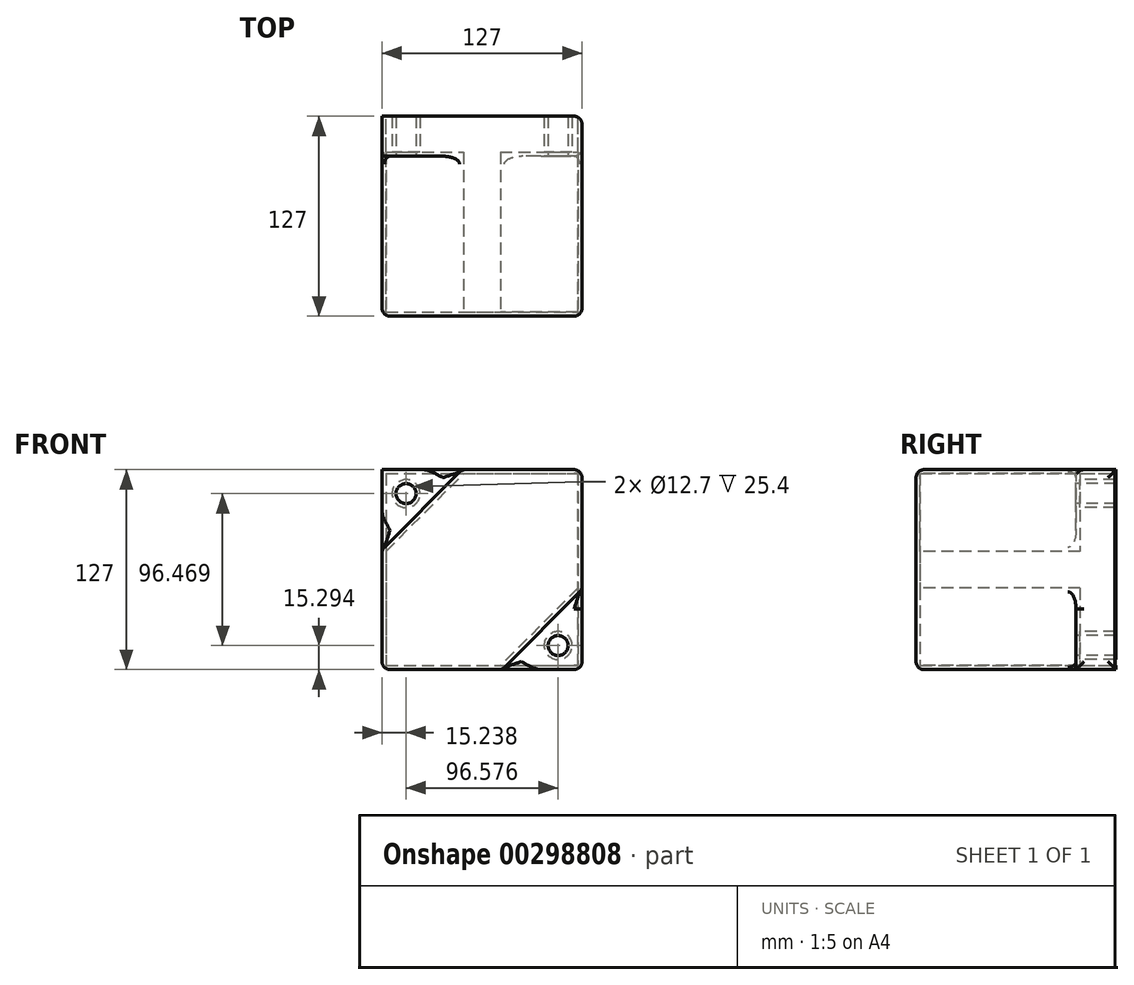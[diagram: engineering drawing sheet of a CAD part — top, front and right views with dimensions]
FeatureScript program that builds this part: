
annotation { "Feature Type Name" : "Feature", "Feature Type Description" : "" }
export const myFeature = defineFeature(function(context is Context, id is Id, definition is map)
    precondition{}
    {
        {
            var Q0;
            Q0=qCreatedBy(makeId("Front.planeOp"),FACE);
            var sketch = newSketch(context, id + "F0", { "sketchPlane" : qUnion([Q0])});
            skLineSegment(sketch, "E0.bottom", {"start": v(-56.8, 80.98) * mm, "end": v(70.2, 80.98) * mm});
            skLineSegment(sketch, "E0.top", {"start": v(-56.8, -46.02) * mm, "end": v(70.2, -46.02) * mm});
            skLineSegment(sketch, "E0.left", {"start": v(-56.8, 80.98) * mm, "end": v(-56.8, -46.02) * mm});
            skLineSegment(sketch, "E0.right", {"start": v(70.2, 80.98) * mm, "end": v(70.2, -46.02) * mm});
            skSolve(sketch);
        }
        {
            var Q0;
            Q0=makeQuery(id+"F0.imprint","IMPRINT",FACE,{"disambiguationData":[TD([[makeQuery(id+"F0.imprint","IMPRINT",EDGE,{"derivedFrom":sQuery(id+"F0.wireOp",EDGE,"E0.bottom")}),-1.0]])]});
            extrude(context, id + "F1", {"entities" : qUnion([Q0]), "depth" : 127 * mm});
        }
        {
            var Q0;
            Q0=makeQuery(id+"F1.opExtrude","CAP_FACE",FACE,{"disambiguationData":[OSD([sQuery(id+"F0.wireOp",EDGE,"E0.bottom"),sQuery(id+"F0.wireOp",EDGE,"E0.top"),sQuery(id+"F0.wireOp",EDGE,"E0.left"),sQuery(id+"F0.wireOp",EDGE,"E0.right")])],"isStart":false});
            var sketch = newSketch(context, id + "F2", { "sketchPlane" : qUnion([Q0])});
            skLineSegment(sketch, "E1", {"start": v(-56.8, 80.98) * mm, "end": v(-56.8, 30.18) * mm});
            skLineSegment(sketch, "E2", {"start": v(-56.8, 30.18) * mm, "end": v(-6, 80.98) * mm});
            skLineSegment(sketch, "E3", {"start": v(-6, 80.98) * mm, "end": v(-56.8, 80.98) * mm});
            skLineSegment(sketch, "E4", {"start": v(19.4, -46.02) * mm, "end": v(70.2, -46.02) * mm});
            skLineSegment(sketch, "E5", {"start": v(70.2, -46.02) * mm, "end": v(70.2, 4.78) * mm});
            skLineSegment(sketch, "E6", {"start": v(70.2, 4.78) * mm, "end": v(19.4, -46.02) * mm});
            skSolve(sketch);
        }
        {
            var Q0;
            Q0=makeQuery(id+"F2.imprint","IMPRINT",FACE,{"disambiguationData":[TD([[makeQuery(id+"F2.imprint","IMPRINT",EDGE,{"derivedFrom":sQuery(id+"F2.wireOp",EDGE,"E1")}),1.0]])]});
            var Q1;
            Q1=makeQuery(id+"F2.imprint","IMPRINT",FACE,{"disambiguationData":[TD([[makeQuery(id+"F2.imprint","IMPRINT",EDGE,{"derivedFrom":sQuery(id+"F2.wireOp",EDGE,"E4")}),1.0]])]});
            extrude(context, id + "F3", {"entities" : qUnion([Q0, Q1]), "operationType" : NewBodyOperationType.REMOVE, "oppositeDirection" : true, "depth" : 101.6 * mm});
        }
        {
            var Q0;
            Q0=makeQuery(id+"F3.boolean.opBoolean","COPY",FACE,{"derivedFrom":makeQuery(id+"F3.opExtrude","CAP_FACE",FACE,{"disambiguationData":[OSD([sQuery(id+"F2.wireOp",EDGE,"E1"),sQuery(id+"F2.wireOp",EDGE,"E2"),sQuery(id+"F2.wireOp",EDGE,"E3")])],"isStart":false})});
            var sketch = newSketch(context, id + "F4", { "sketchPlane" : qUnion([Q0])});
            skCircle(sketch, "E7", {"center": v(-41.56, 65.74) * mm, "radius": 6.35 * mm});
            skPoint(sketch, "E8.end.orphan", {"position": v(-41.56, 80.98) * mm});
            skCircle(sketch, "E9", {"center": v(55.01, -30.73) * mm, "radius": 6.35 * mm});
            skPoint(sketch, "E10.end.orphan", {"position": v(70.25, -30.73) * mm});
            skSolve(sketch);
        }
        {
            var Q0;
            Q0=makeQuery(id+"F4.imprint","IMPRINT",FACE,{"disambiguationData":[TD([[makeQuery(id+"F4.imprint","IMPRINT",EDGE,{"derivedFrom":sQuery(id+"F4.wireOp",EDGE,"E7")}),1.0]])]});
            var Q1;
            Q1=makeQuery(id+"F4.imprint","IMPRINT",FACE,{"disambiguationData":[TD([[makeQuery(id+"F4.imprint","IMPRINT",EDGE,{"derivedFrom":sQuery(id+"F4.wireOp",EDGE,"E9")}),1.0]])]});
            extrude(context, id + "F5", {"entities" : qUnion([Q0, Q1]), "operationType" : NewBodyOperationType.REMOVE, "endBound" : BoundingType.THROUGH_ALL, "oppositeDirection" : true, "depth" : 25.4 * mm});
        }
        {
            var Q0;
            Q0=makeQuery(id+"F1.opExtrude","CAP_FACE",FACE,{"disambiguationData":[OSD([sQuery(id+"F0.wireOp",EDGE,"E0.bottom"),sQuery(id+"F0.wireOp",EDGE,"E0.top"),sQuery(id+"F0.wireOp",EDGE,"E0.left"),sQuery(id+"F0.wireOp",EDGE,"E0.right")])],"isStart":true});
            shell(context, id + "F6", {"entities" : qUnion([Q0]), "thickness" : 2.54 * mm});
        }
        {
            var Q0;
            Q0=makeQuery(id+"F1.opExtrude","CAP_FACE",FACE,{"disambiguationData":[OSD([sQuery(id+"F0.wireOp",EDGE,"E0.bottom"),sQuery(id+"F0.wireOp",EDGE,"E0.top"),sQuery(id+"F0.wireOp",EDGE,"E0.left"),sQuery(id+"F0.wireOp",EDGE,"E0.right")])],"isStart":false});
            var Q1;
            Q1=makeQuery(id+"F3.boolean.opBoolean","COPY",FACE,{"derivedFrom":makeQuery(id+"F3.opExtrude","SWEPT_FACE",FACE,{"disambiguationData":[OSD([sQuery(id+"F2.wireOp",EDGE,"E6")])]})});
            var Q2;
            Q2=makeQuery(id+"F1.opExtrude","SWEPT_FACE",FACE,{"disambiguationData":[OSD([sQuery(id+"F0.wireOp",EDGE,"E0.right")])]});
            var Q3;
            Q3=makeQuery(id+"F1.opExtrude","SWEPT_EDGE",EDGE,{"disambiguationData":[OSD([sQuery(id+"F0.wireOp",EDGE,"E0.top"),sQuery(id+"F0.wireOp",EDGE,"E0.left")])]});
            var Q4;
            Q4=makeQuery(id+"F3.boolean.opBoolean","COPY",FACE,{"derivedFrom":makeQuery(id+"F3.opExtrude","SWEPT_FACE",FACE,{"disambiguationData":[OSD([sQuery(id+"F2.wireOp",EDGE,"E2")])]})});
            fillet(context, id + "F7", {"entities" : qUnion([Q0, Q1, Q2, Q3, Q4]), "radius" : 5.08 * mm, "tangentPropagation" : true, "allowEdgeOverflow" : false});
        }
    });
